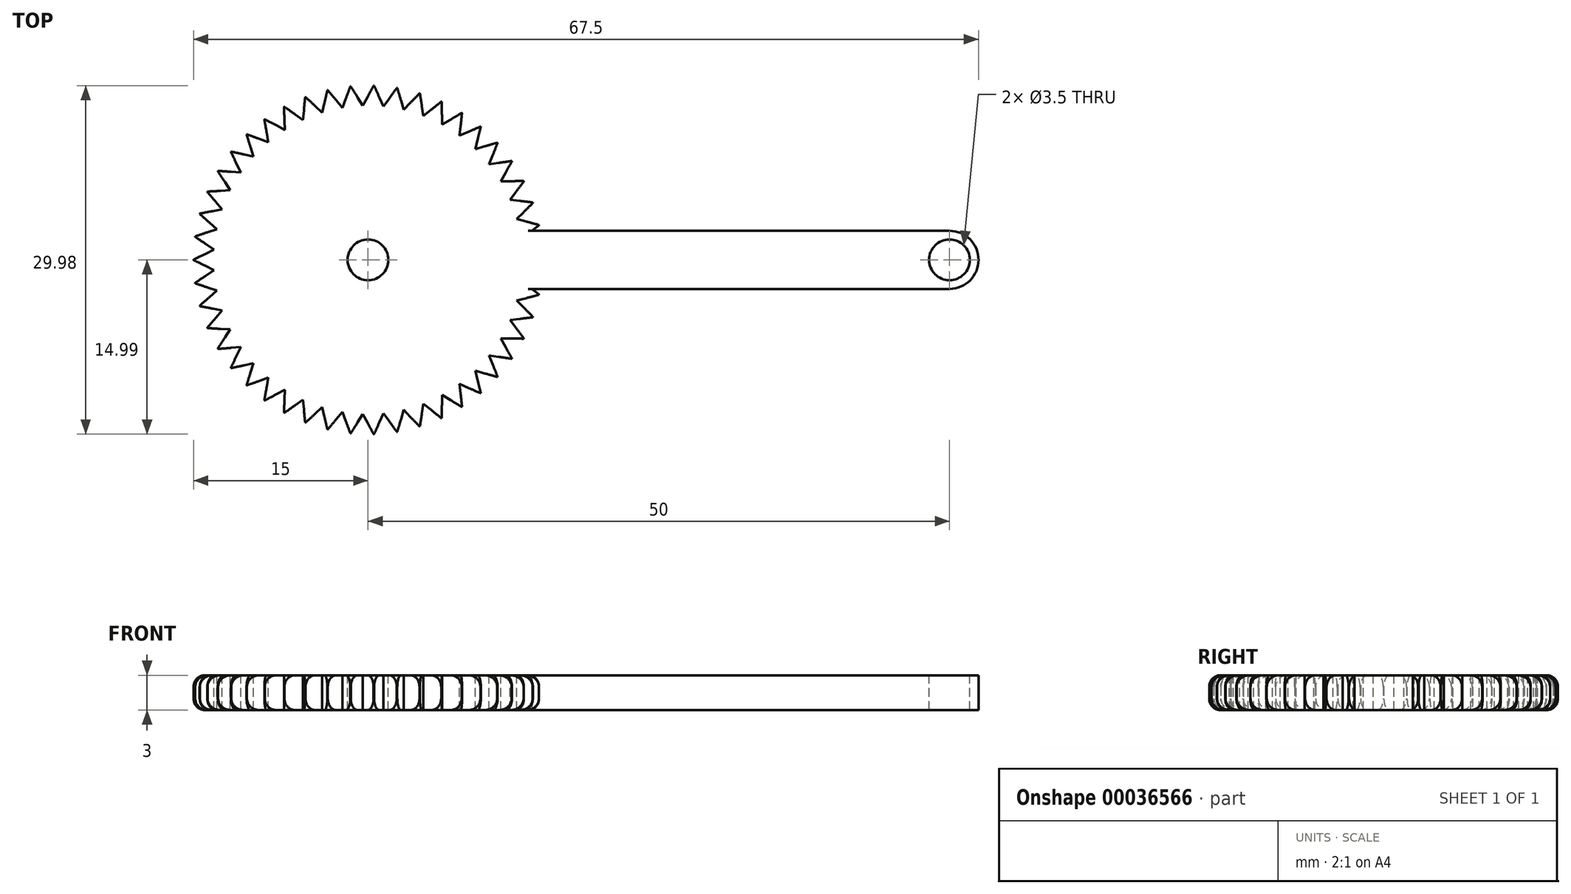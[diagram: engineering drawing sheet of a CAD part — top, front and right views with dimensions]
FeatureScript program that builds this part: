
annotation { "Feature Type Name" : "Feature", "Feature Type Description" : "" }
export const myFeature = defineFeature(function(context is Context, id is Id, definition is map)
    precondition{}
    {
        {
            var Q0;
            Q0=qCreatedBy(makeId("Top.planeOp"),FACE);
            var sketch = newSketch(context, id + "F0", { "sketchPlane" : qUnion([Q0])});
            skCircle(sketch, "E0", {"center": v(0, 0) * mm, "radius": 15 * mm});
            skSolve(sketch);
        }
        {
            var Q0;
            Q0 = qSketchRegion(id + "F0", true);
            extrude(context, id + "F1", {"entities" : qUnion([Q0]), "depth" : 3 * mm});
        }
        {
            var Q0;
            Q0=makeQuery(id+"F1.opExtrude","CAP_EDGE",EDGE,{"disambiguationData":[OSD([sQuery(id+"F0.wireOp",EDGE,"E0")])],"isStart":false});
            var Q1;
            Q1=makeQuery(id+"F1.opExtrude","CAP_EDGE",EDGE,{"disambiguationData":[OSD([sQuery(id+"F0.wireOp",EDGE,"E0")])],"isStart":true});
            fillet(context, id + "F2", {"entities" : qUnion([Q0, Q1]), "radius" : 1 * mm, "tangentPropagation" : true, "allowEdgeOverflow" : false});
        }
        {
            var Q0;
            Q0=makeQuery(id+"F1.opExtrude","CAP_FACE",FACE,{"disambiguationData":[OSD([sQuery(id+"F0.wireOp",EDGE,"E0")])],"isStart":false});
            var sketch = newSketch(context, id + "F3", { "sketchPlane" : qUnion([Q0])});
            skCircle(sketch, "E1.cCircle", {"center": v(14.42, 0) * mm, "radius": 0.58 * mm, "construction": true});
            skLineSegment(sketch, "E1.0", {"start": v(15, 1) * mm, "end": v(15, -1) * mm});
            skLineSegment(sketch, "E1.1", {"start": v(15, -1) * mm, "end": v(13.27, 0) * mm});
            skLineSegment(sketch, "E1.2", {"start": v(13.27, 0) * mm, "end": v(15, 1) * mm});
            skPoint(sketch, "E2", {"position": v(15, 0) * mm});
            skLineSegment(sketch, "E3.1.0", {"start": v(13.15, 1.77) * mm, "end": v(14.73, 3) * mm});
            skLineSegment(sketch, "E3.1.1", {"start": v(14.73, 3) * mm, "end": v(15, 1) * mm});
            skLineSegment(sketch, "E3.1.2", {"start": v(15, 1) * mm, "end": v(13.15, 1.77) * mm});
            skLineSegment(sketch, "E3.2.0", {"start": v(12.8, 3.5) * mm, "end": v(14.2, 4.93) * mm});
            skLineSegment(sketch, "E3.2.1", {"start": v(14.2, 4.93) * mm, "end": v(14.73, 3) * mm});
            skLineSegment(sketch, "E3.2.2", {"start": v(14.73, 3) * mm, "end": v(12.8, 3.5) * mm});
            skLineSegment(sketch, "E3.3.0", {"start": v(12.22, 5.18) * mm, "end": v(13.42, 6.78) * mm});
            skLineSegment(sketch, "E3.3.1", {"start": v(13.42, 6.78) * mm, "end": v(14.2, 4.94) * mm});
            skLineSegment(sketch, "E3.3.2", {"start": v(14.2, 4.94) * mm, "end": v(12.22, 5.18) * mm});
            skLineSegment(sketch, "E3.4.0", {"start": v(11.42, 6.76) * mm, "end": v(12.4, 8.5) * mm});
            skLineSegment(sketch, "E3.4.1", {"start": v(12.4, 8.5) * mm, "end": v(13.42, 6.78) * mm});
            skLineSegment(sketch, "E3.4.2", {"start": v(13.42, 6.78) * mm, "end": v(11.42, 6.76) * mm});
            skLineSegment(sketch, "E3.5.0", {"start": v(10.41, 8.22) * mm, "end": v(11.15, 10.08) * mm});
            skLineSegment(sketch, "E3.5.1", {"start": v(11.15, 10.08) * mm, "end": v(12.4, 8.51) * mm});
            skLineSegment(sketch, "E3.5.2", {"start": v(12.4, 8.51) * mm, "end": v(10.41, 8.22) * mm});
            skLineSegment(sketch, "E3.6.0", {"start": v(9.22, 9.54) * mm, "end": v(9.7, 11.48) * mm});
            skLineSegment(sketch, "E3.6.1", {"start": v(9.7, 11.48) * mm, "end": v(11.15, 10.09) * mm});
            skLineSegment(sketch, "E3.6.2", {"start": v(11.15, 10.09) * mm, "end": v(9.22, 9.54) * mm});
            skLineSegment(sketch, "E3.7.0", {"start": v(7.87, 10.68) * mm, "end": v(8.1, 12.67) * mm});
            skLineSegment(sketch, "E3.7.1", {"start": v(8.1, 12.67) * mm, "end": v(9.7, 11.48) * mm});
            skLineSegment(sketch, "E3.7.2", {"start": v(9.7, 11.48) * mm, "end": v(7.87, 10.68) * mm});
            skLineSegment(sketch, "E3.8.0", {"start": v(6.38, 11.64) * mm, "end": v(6.33, 13.63) * mm});
            skLineSegment(sketch, "E3.8.1", {"start": v(6.33, 13.63) * mm, "end": v(8.09, 12.67) * mm});
            skLineSegment(sketch, "E3.8.2", {"start": v(8.09, 12.67) * mm, "end": v(6.38, 11.64) * mm});
            skLineSegment(sketch, "E3.9.0", {"start": v(4.77, 12.38) * mm, "end": v(4.46, 14.36) * mm});
            skLineSegment(sketch, "E3.9.1", {"start": v(4.46, 14.36) * mm, "end": v(6.32, 13.64) * mm});
            skLineSegment(sketch, "E3.9.2", {"start": v(6.32, 13.64) * mm, "end": v(4.77, 12.38) * mm});
            skLineSegment(sketch, "E3.10.0", {"start": v(3.08, 12.9) * mm, "end": v(2.5, 14.82) * mm});
            skLineSegment(sketch, "E3.10.1", {"start": v(2.5, 14.82) * mm, "end": v(4.45, 14.36) * mm});
            skLineSegment(sketch, "E3.10.2", {"start": v(4.45, 14.36) * mm, "end": v(3.08, 12.9) * mm});
            skLineSegment(sketch, "E3.11.0", {"start": v(1.33, 13.2) * mm, "end": v(0.5, 15.02) * mm});
            skLineSegment(sketch, "E3.11.1", {"start": v(0.5, 15.02) * mm, "end": v(2.5, 14.82) * mm});
            skLineSegment(sketch, "E3.11.2", {"start": v(2.5, 14.82) * mm, "end": v(1.33, 13.2) * mm});
            skLineSegment(sketch, "E3.12.0", {"start": v(-0.44, 13.26) * mm, "end": v(-1.5, 14.96) * mm});
            skLineSegment(sketch, "E3.12.1", {"start": v(-1.5, 14.96) * mm, "end": v(0.5, 15.03) * mm});
            skLineSegment(sketch, "E3.12.2", {"start": v(0.5, 15.03) * mm, "end": v(-0.44, 13.26) * mm});
            skLineSegment(sketch, "E3.13.0", {"start": v(-2.2, 13.08) * mm, "end": v(-3.48, 14.62) * mm});
            skLineSegment(sketch, "E3.13.1", {"start": v(-3.48, 14.62) * mm, "end": v(-1.5, 14.96) * mm});
            skLineSegment(sketch, "E3.13.2", {"start": v(-1.5, 14.96) * mm, "end": v(-2.2, 13.08) * mm});
            skLineSegment(sketch, "E3.14.0", {"start": v(-3.93, 12.67) * mm, "end": v(-5.4, 14.03) * mm});
            skLineSegment(sketch, "E3.14.1", {"start": v(-5.4, 14.03) * mm, "end": v(-3.49, 14.62) * mm});
            skLineSegment(sketch, "E3.14.2", {"start": v(-3.49, 14.62) * mm, "end": v(-3.93, 12.67) * mm});
            skLineSegment(sketch, "E3.15.0", {"start": v(-5.58, 12.04) * mm, "end": v(-7.22, 13.19) * mm});
            skLineSegment(sketch, "E3.15.1", {"start": v(-7.22, 13.19) * mm, "end": v(-5.4, 14.03) * mm});
            skLineSegment(sketch, "E3.15.2", {"start": v(-5.4, 14.03) * mm, "end": v(-5.58, 12.04) * mm});
            skLineSegment(sketch, "E3.16.0", {"start": v(-7.14, 11.18) * mm, "end": v(-8.91, 12.1) * mm});
            skLineSegment(sketch, "E3.16.1", {"start": v(-8.91, 12.1) * mm, "end": v(-7.23, 13.18) * mm});
            skLineSegment(sketch, "E3.16.2", {"start": v(-7.23, 13.18) * mm, "end": v(-7.14, 11.18) * mm});
            skLineSegment(sketch, "E3.17.0", {"start": v(-8.57, 10.13) * mm, "end": v(-10.45, 10.8) * mm});
            skLineSegment(sketch, "E3.17.1", {"start": v(-10.45, 10.8) * mm, "end": v(-8.92, 12.1) * mm});
            skLineSegment(sketch, "E3.17.2", {"start": v(-8.92, 12.1) * mm, "end": v(-8.57, 10.13) * mm});
            skLineSegment(sketch, "E3.18.0", {"start": v(-9.84, 8.9) * mm, "end": v(-11.8, 9.32) * mm});
            skLineSegment(sketch, "E3.18.1", {"start": v(-11.8, 9.32) * mm, "end": v(-10.45, 10.8) * mm});
            skLineSegment(sketch, "E3.18.2", {"start": v(-10.45, 10.8) * mm, "end": v(-9.84, 8.9) * mm});
            skLineSegment(sketch, "E3.19.0", {"start": v(-10.94, 7.5) * mm, "end": v(-12.93, 7.66) * mm});
            skLineSegment(sketch, "E3.19.1", {"start": v(-12.93, 7.66) * mm, "end": v(-11.8, 9.31) * mm});
            skLineSegment(sketch, "E3.19.2", {"start": v(-11.8, 9.31) * mm, "end": v(-10.94, 7.5) * mm});
            skLineSegment(sketch, "E3.20.0", {"start": v(-11.84, 5.98) * mm, "end": v(-13.84, 5.87) * mm});
            skLineSegment(sketch, "E3.20.1", {"start": v(-13.84, 5.87) * mm, "end": v(-12.94, 7.66) * mm});
            skLineSegment(sketch, "E3.20.2", {"start": v(-12.94, 7.66) * mm, "end": v(-11.84, 5.98) * mm});
            skLineSegment(sketch, "E3.21.0", {"start": v(-12.53, 4.35) * mm, "end": v(-14.5, 3.98) * mm});
            skLineSegment(sketch, "E3.21.1", {"start": v(-14.5, 3.98) * mm, "end": v(-13.84, 5.87) * mm});
            skLineSegment(sketch, "E3.21.2", {"start": v(-13.84, 5.87) * mm, "end": v(-12.53, 4.35) * mm});
            skLineSegment(sketch, "E3.22.0", {"start": v(-13, 2.64) * mm, "end": v(-14.9, 2) * mm});
            skLineSegment(sketch, "E3.22.1", {"start": v(-14.9, 2) * mm, "end": v(-14.5, 3.97) * mm});
            skLineSegment(sketch, "E3.22.2", {"start": v(-14.5, 3.97) * mm, "end": v(-13, 2.64) * mm});
            skLineSegment(sketch, "E3.23.0", {"start": v(-13.24, 0.89) * mm, "end": v(-15.03, 0) * mm});
            skLineSegment(sketch, "E3.23.1", {"start": v(-15.03, 0) * mm, "end": v(-14.9, 2) * mm});
            skLineSegment(sketch, "E3.23.2", {"start": v(-14.9, 2) * mm, "end": v(-13.24, 0.89) * mm});
            skLineSegment(sketch, "E3.24.0", {"start": v(-13.24, -0.89) * mm, "end": v(-14.9, -2) * mm});
            skLineSegment(sketch, "E3.24.1", {"start": v(-14.9, -2) * mm, "end": v(-15.03, 0) * mm});
            skLineSegment(sketch, "E3.24.2", {"start": v(-15.03, 0) * mm, "end": v(-13.24, -0.89) * mm});
            skLineSegment(sketch, "E3.25.0", {"start": v(-13, -2.64) * mm, "end": v(-14.5, -3.97) * mm});
            skLineSegment(sketch, "E3.25.1", {"start": v(-14.5, -3.97) * mm, "end": v(-14.9, -2) * mm});
            skLineSegment(sketch, "E3.25.2", {"start": v(-14.9, -2) * mm, "end": v(-13, -2.64) * mm});
            skLineSegment(sketch, "E3.26.0", {"start": v(-12.53, -4.35) * mm, "end": v(-13.84, -5.87) * mm});
            skLineSegment(sketch, "E3.26.1", {"start": v(-13.84, -5.87) * mm, "end": v(-14.5, -3.98) * mm});
            skLineSegment(sketch, "E3.26.2", {"start": v(-14.5, -3.98) * mm, "end": v(-12.53, -4.35) * mm});
            skLineSegment(sketch, "E3.27.0", {"start": v(-11.84, -5.98) * mm, "end": v(-12.94, -7.66) * mm});
            skLineSegment(sketch, "E3.27.1", {"start": v(-12.94, -7.66) * mm, "end": v(-13.84, -5.87) * mm});
            skLineSegment(sketch, "E3.27.2", {"start": v(-13.84, -5.87) * mm, "end": v(-11.84, -5.98) * mm});
            skLineSegment(sketch, "E3.28.0", {"start": v(-10.94, -7.5) * mm, "end": v(-11.8, -9.31) * mm});
            skLineSegment(sketch, "E3.28.1", {"start": v(-11.8, -9.31) * mm, "end": v(-12.93, -7.66) * mm});
            skLineSegment(sketch, "E3.28.2", {"start": v(-12.93, -7.66) * mm, "end": v(-10.94, -7.5) * mm});
            skLineSegment(sketch, "E3.29.0", {"start": v(-9.84, -8.9) * mm, "end": v(-10.45, -10.8) * mm});
            skLineSegment(sketch, "E3.29.1", {"start": v(-10.45, -10.8) * mm, "end": v(-11.8, -9.32) * mm});
            skLineSegment(sketch, "E3.29.2", {"start": v(-11.8, -9.32) * mm, "end": v(-9.84, -8.9) * mm});
            skLineSegment(sketch, "E3.30.0", {"start": v(-8.57, -10.13) * mm, "end": v(-8.92, -12.1) * mm});
            skLineSegment(sketch, "E3.30.1", {"start": v(-8.92, -12.1) * mm, "end": v(-10.45, -10.8) * mm});
            skLineSegment(sketch, "E3.30.2", {"start": v(-10.45, -10.8) * mm, "end": v(-8.57, -10.13) * mm});
            skLineSegment(sketch, "E3.31.0", {"start": v(-7.14, -11.18) * mm, "end": v(-7.23, -13.18) * mm});
            skLineSegment(sketch, "E3.31.1", {"start": v(-7.23, -13.18) * mm, "end": v(-8.91, -12.1) * mm});
            skLineSegment(sketch, "E3.31.2", {"start": v(-8.91, -12.1) * mm, "end": v(-7.14, -11.18) * mm});
            skLineSegment(sketch, "E3.32.0", {"start": v(-5.58, -12.04) * mm, "end": v(-5.4, -14.03) * mm});
            skLineSegment(sketch, "E3.32.1", {"start": v(-5.4, -14.03) * mm, "end": v(-7.22, -13.19) * mm});
            skLineSegment(sketch, "E3.32.2", {"start": v(-7.22, -13.19) * mm, "end": v(-5.58, -12.04) * mm});
            skLineSegment(sketch, "E3.33.0", {"start": v(-3.93, -12.67) * mm, "end": v(-3.49, -14.62) * mm});
            skLineSegment(sketch, "E3.33.1", {"start": v(-3.49, -14.62) * mm, "end": v(-5.4, -14.03) * mm});
            skLineSegment(sketch, "E3.33.2", {"start": v(-5.4, -14.03) * mm, "end": v(-3.93, -12.67) * mm});
            skLineSegment(sketch, "E3.34.0", {"start": v(-2.2, -13.08) * mm, "end": v(-1.5, -14.96) * mm});
            skLineSegment(sketch, "E3.34.1", {"start": v(-1.5, -14.96) * mm, "end": v(-3.48, -14.62) * mm});
            skLineSegment(sketch, "E3.34.2", {"start": v(-3.48, -14.62) * mm, "end": v(-2.2, -13.08) * mm});
            skLineSegment(sketch, "E3.35.0", {"start": v(-0.44, -13.26) * mm, "end": v(0.5, -15.03) * mm});
            skLineSegment(sketch, "E3.35.1", {"start": v(0.5, -15.03) * mm, "end": v(-1.5, -14.96) * mm});
            skLineSegment(sketch, "E3.35.2", {"start": v(-1.5, -14.96) * mm, "end": v(-0.44, -13.26) * mm});
            skLineSegment(sketch, "E3.36.0", {"start": v(1.33, -13.2) * mm, "end": v(2.5, -14.82) * mm});
            skLineSegment(sketch, "E3.36.1", {"start": v(2.5, -14.82) * mm, "end": v(0.5, -15.02) * mm});
            skLineSegment(sketch, "E3.36.2", {"start": v(0.5, -15.02) * mm, "end": v(1.33, -13.2) * mm});
            skLineSegment(sketch, "E3.37.0", {"start": v(3.08, -12.9) * mm, "end": v(4.45, -14.36) * mm});
            skLineSegment(sketch, "E3.37.1", {"start": v(4.45, -14.36) * mm, "end": v(2.5, -14.82) * mm});
            skLineSegment(sketch, "E3.37.2", {"start": v(2.5, -14.82) * mm, "end": v(3.08, -12.9) * mm});
            skLineSegment(sketch, "E3.38.0", {"start": v(4.77, -12.38) * mm, "end": v(6.32, -13.64) * mm});
            skLineSegment(sketch, "E3.38.1", {"start": v(6.32, -13.64) * mm, "end": v(4.46, -14.36) * mm});
            skLineSegment(sketch, "E3.38.2", {"start": v(4.46, -14.36) * mm, "end": v(4.77, -12.38) * mm});
            skLineSegment(sketch, "E3.39.0", {"start": v(6.38, -11.64) * mm, "end": v(8.09, -12.67) * mm});
            skLineSegment(sketch, "E3.39.1", {"start": v(8.09, -12.67) * mm, "end": v(6.33, -13.63) * mm});
            skLineSegment(sketch, "E3.39.2", {"start": v(6.33, -13.63) * mm, "end": v(6.38, -11.64) * mm});
            skLineSegment(sketch, "E3.40.0", {"start": v(7.87, -10.68) * mm, "end": v(9.7, -11.48) * mm});
            skLineSegment(sketch, "E3.40.1", {"start": v(9.7, -11.48) * mm, "end": v(8.1, -12.67) * mm});
            skLineSegment(sketch, "E3.40.2", {"start": v(8.1, -12.67) * mm, "end": v(7.87, -10.68) * mm});
            skLineSegment(sketch, "E3.41.0", {"start": v(9.22, -9.54) * mm, "end": v(11.15, -10.09) * mm});
            skLineSegment(sketch, "E3.41.1", {"start": v(11.15, -10.09) * mm, "end": v(9.7, -11.48) * mm});
            skLineSegment(sketch, "E3.41.2", {"start": v(9.7, -11.48) * mm, "end": v(9.22, -9.54) * mm});
            skLineSegment(sketch, "E3.42.0", {"start": v(10.41, -8.22) * mm, "end": v(12.4, -8.51) * mm});
            skLineSegment(sketch, "E3.42.1", {"start": v(12.4, -8.51) * mm, "end": v(11.15, -10.08) * mm});
            skLineSegment(sketch, "E3.42.2", {"start": v(11.15, -10.08) * mm, "end": v(10.41, -8.22) * mm});
            skLineSegment(sketch, "E3.43.0", {"start": v(11.42, -6.76) * mm, "end": v(13.42, -6.78) * mm});
            skLineSegment(sketch, "E3.43.1", {"start": v(13.42, -6.78) * mm, "end": v(12.4, -8.5) * mm});
            skLineSegment(sketch, "E3.43.2", {"start": v(12.4, -8.5) * mm, "end": v(11.42, -6.76) * mm});
            skLineSegment(sketch, "E3.44.0", {"start": v(12.22, -5.18) * mm, "end": v(14.2, -4.94) * mm});
            skLineSegment(sketch, "E3.44.1", {"start": v(14.2, -4.94) * mm, "end": v(13.42, -6.78) * mm});
            skLineSegment(sketch, "E3.44.2", {"start": v(13.42, -6.78) * mm, "end": v(12.22, -5.18) * mm});
            skLineSegment(sketch, "E3.45.0", {"start": v(12.8, -3.5) * mm, "end": v(14.73, -3) * mm});
            skLineSegment(sketch, "E3.45.1", {"start": v(14.73, -3) * mm, "end": v(14.2, -4.93) * mm});
            skLineSegment(sketch, "E3.45.2", {"start": v(14.2, -4.93) * mm, "end": v(12.8, -3.5) * mm});
            skLineSegment(sketch, "E3.46.0", {"start": v(13.15, -1.77) * mm, "end": v(15, -1) * mm});
            skLineSegment(sketch, "E3.46.1", {"start": v(15, -1) * mm, "end": v(14.73, -3) * mm});
            skLineSegment(sketch, "E3.46.2", {"start": v(14.73, -3) * mm, "end": v(13.15, -1.77) * mm});
            skPoint(sketch, "E3.center", {"position": v(0, 0) * mm});
            skSolve(sketch);
        }
        {
            var Q0;
            Q0 = qSketchRegion(id + "F3", true);
            extrude(context, id + "F4", {"entities" : qUnion([Q0]), "operationType" : NewBodyOperationType.REMOVE, "oppositeDirection" : true, "depth" : 3 * mm});
        }
        {
            var Q0;
            Q0=makeQuery(id+"F1.opExtrude","CAP_FACE",FACE,{"disambiguationData":[OSD([sQuery(id+"F0.wireOp",EDGE,"E0")])],"isStart":false});
            var sketch = newSketch(context, id + "F5", { "sketchPlane" : qUnion([Q0])});
            skLineSegment(sketch, "E4.bottom", {"start": v(0, -2.5) * mm, "end": v(50, -2.5) * mm});
            skLineSegment(sketch, "E4.top", {"start": v(0, 2.5) * mm, "end": v(50, 2.5) * mm});
            skLineSegment(sketch, "E4.left", {"start": v(0, -2.5) * mm, "end": v(0, 2.5) * mm});
            skArc(sketch, "E5", {"start": v(50, -2.5) * mm, "mid": v(52.5, 0) * mm, "end": v(50, 2.5) * mm});
            skCircle(sketch, "E6", {"center": v(50, 0) * mm, "radius": 1.75 * mm});
            skSolve(sketch);
        }
        {
            var Q0;
            Q0 = qSketchRegion(id + "F5", true);
            extrude(context, id + "F6", {"entities" : qUnion([Q0]), "operationType" : NewBodyOperationType.ADD, "oppositeDirection" : true, "depth" : 3 * mm});
        }
        {
            var Q0;
            Q0=makeQuery(id+"F6.boolean.opBoolean","MERGE",FACE,{"derivedFrom":[makeQuery(id+"F1.opExtrude","CAP_FACE",FACE,{"disambiguationData":[OSD([sQuery(id+"F0.wireOp",EDGE,"E0")])],"isStart":false}),makeQuery(id+"F6.opExtrude","CAP_FACE",FACE,{"disambiguationData":[OSD([sQuery(id+"F5.wireOp",EDGE,"E4.bottom"),sQuery(id+"F5.wireOp",EDGE,"E4.top"),sQuery(id+"F5.wireOp",EDGE,"E4.left"),sQuery(id+"F5.wireOp",EDGE,"E5"),sQuery(id+"F5.wireOp",EDGE,"E6")])],"isStart":true})]});
            var sketch = newSketch(context, id + "F7", { "sketchPlane" : qUnion([Q0])});
            skCircle(sketch, "E7", {"center": v(0, 0) * mm, "radius": 1.75 * mm});
            skSolve(sketch);
        }
        {
            var Q0;
            Q0 = qSketchRegion(id + "F7", true);
            extrude(context, id + "F8", {"entities" : qUnion([Q0]), "operationType" : NewBodyOperationType.REMOVE, "endBound" : BoundingType.THROUGH_ALL, "oppositeDirection" : true, "depth" : 25 * mm});
        }
    });
